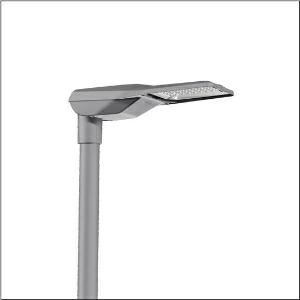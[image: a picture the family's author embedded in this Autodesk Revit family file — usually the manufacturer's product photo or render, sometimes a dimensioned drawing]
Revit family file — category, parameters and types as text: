
# Revit family: streetlight_sl_21_iq_mini___p1_0a_5xe2a41g08gb_a1a0
name_source: partatom
category: Lighting Fixtures
units: mm (PartAtom-declared; Revit-internal decimal feet)

## family parameters
Cut with Voids When Loaded = No
Host = Face
Light Source = No
Part Type = Normal
Room Calculation Point = No
Round Connector Dimension = Use Diameter
Shared = No

## types (1)
- --- (1 x LED, 5920 lm, 37.1 W, 4000K)
    Apparent Load = 37 VA
    CIE Flux Codes = 21 50 90 100 100
    Color Rendering = 70
    Color Temperature = 4000K
    Default Elevation = 1800 mm
    Description = Streetlight SL 21 iQ mini, mast luminaire, primary light control with lens, of PMMA, primary optical cover: cover, of toughened safety glass, transparent, light distribution: P1.0a, light emission: direct distribution, primary light characteristic: asymmetric, installation type: post-top, side-entry, LED, High Power LED, rated luminous flux: 5.920lm, luminous efficacy: 160lm/W, light colour: 740, colour temperature: 4000K, control: Street-Remote, Auto-Match, Temp-Guard, Lumen-Switch, Night-Set, Smart-Wire, Light-Fading, Desk-Remote (wireless, voltage-free reading and setting of iQ features in the workshop via application-optimized NFC function/RFID function), optimised constant luminous flux control (CLO 2.0), presetting dimming linear, mains connection: 220..240V, AC, 50/60Hz, start of lifetime: 37W, end of service life: 39W, reduction: 18W, luminaire housing, of diecast aluminium, powder-coated, Siteco® metallic grey (DB 702S), corrosivity category C5 mid according to DIN EN ISO 12944, please order mast flange separately, inclination adjustable: 0°, 5°, 10°, 15°, sealing non-destructively replaceable, multi-level sealing system, length: 628mm, width: 235mm, height: 110mm, mast flange for spigot size: 42mm (side-entry): 5XC10008XM4, 60/48mm (side-entry/post-top): 5XC10108XM2, 76/60mm (side-entry/post-top): 5XC10108XM1, protection rating (complete): IP66, insulation class (complete): insulation class II (safety insulation), certification: CE, ENEC, ENEC+, VDE, impact resistance: IK09, permissible operating ambient temperature for outdoor applications: -40..+50°C, standard-compliant lighting for roads and squares, packaging unit: 1 piece

Light Distribution: P1.0a
    Height = 110 mm
    Lamp = 1 x LED
    Lamp Light Flux = 5920 lm
    Lamp Power = 37.1 W
    Lamp count = 1
    Length = 625 mm
    Luminous efficacy = 160 lm/W
    Manufacturer = Siteco
    ModVariant = No
    Model = 5XE2A41G08GB
    Number of Poles = 1
    OnlyDefault = Yes
    Power Factor = 1
    Product Name = Streetlight SL 21 iQ mini | P1.0a
    Product group = mast luminaire | pylon top
    ProductGroupID = 6100
    Protection Class = Protection class II
    Protection Degree = IP 66
    RLX_Detail_Level = 1
    RLX_Emergency_Light_Flux = 0 lm
    RLX_Emergency_Type = 0
    RLX_Emergency_Type_DB = No
    RlxData = <blob elided: 103593 chars, md5=196bc4e0>
    Socket = socket
    Standby Power = 0 W
    System Light Flux = 5920 lm
    System Power = 37 W
    Type Comments = factory setting: luminous flux: 100 % | dim-lin: 254 | 385 mA
    Type Image = l_1003519.jpg
    URL = http://relux.com
    VarID = @adj_120237
    Voltage = 0 V
    Weight = 0.00 kg
    Width = 234 mm

## geometry (parser evidence)
native form markers: Blend x4, Sweep x11
no freeform markers — native parametric forms only
